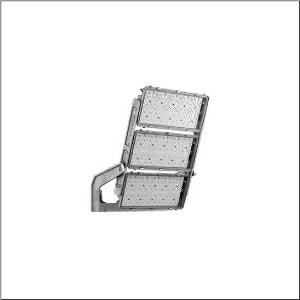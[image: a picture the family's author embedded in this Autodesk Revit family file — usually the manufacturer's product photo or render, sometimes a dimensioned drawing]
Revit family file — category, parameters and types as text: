
# Revit family: floodlight_fl_11_maxi_pro_remote___pl33t_5xa779427f01ba_72f0
name_source: partatom
category: Lighting Fixtures
units: mm (PartAtom-declared; Revit-internal decimal feet)

## family parameters
Cut with Voids When Loaded = No
Host = Face
Light Source = No
Part Type = Normal
Room Calculation Point = No
Round Connector Dimension = Use Diameter
Shared = No

## types (1)
- --- (1 x LED, 132850 lm, 953.7 W, 5000K)
    Apparent Load = 954 VA
    CIE Flux Codes = 25 74 99 100 100
    Color Rendering = 70
    Color Temperature = 5000K
    Default Elevation = 1800 mm
    Description = Floodlight FL 11  maxi  pro Remote floodlight; light control with lens of PMMA; cover panel of toughened safety glass, transparent; light distribution: PL33T, asymmetric direct distribution, LED; colour temperature: 5000K, rated luminous flux: 132.850lm, colour rendering: CRI > 70, light colour: 750; luminous efficacy: 139lm/W; brightness control: DALI 2 (1 DALI address); with terminal, 8-pole, max. 2.5mm², mains connection: 220..240V/380..400V AC, 50/60Hz, surge voltage resistance: line to ground: 10kV, ECG replaceable separately, no afterglow with DALI off / DMX off command, LED unit replaceable without ESD environment, dustproof LED module, dimming range 10..100%; 954W floodlight with 2x LED unit of diecast aluminium, coated grey; length: 713mm / width: 651mm / height: 338mm; mounting bracket, of diecast aluminium, uncoated, natural, equipment: Longlife, protection rating (complete): IP66; insulation class (complete): insulation class I (protective earthing); certification: CE, ENEC, VDE; ball protection: ball impact resistance with accessories, impact resistance: IK07; only for outdoor installations, rated ambient temperature 10°C, permissible operating ambient temperature: -40..+30°C, permissible storage temperature: -40..+85°Cpackaging unit: 1 piece

Light Distribution: PL33T
    Height = 320 mm
    Lamp = 1 x LED
    Lamp Light Flux = 132850 lm
    Lamp Power = 953.7 W
    Lamp count = 1
    Length = 1002 mm
    Luminous efficacy = 139 lm/W
    Manufacturer = Siteco
    ModVariant = No
    Model = 5XA779427F01BA
    Mounting Place = Ceiling
    Mounting Type = Surface mounted
    Number of Poles = 1
    OnlyDefault = Yes
    Power Factor = 1
    Product Name = Floodlight FL 11 maxi pro Remote | PL33T
    Product group = floodlight | ceiling mounted
    ProductGroupID = 302
    Protection Class = Protection class I
    Protection Degree = IP 66
    RLX_Detail_Level = 1
    RLX_Emergency_Light_Flux = 0 lm
    RLX_Emergency_Type = 0
    RLX_Emergency_Type_DB = No
    RlxData = <blob elided: 52289 chars, md5=9290f567>
    Socket = socket
    Standby Power = 0 W
    System Light Flux = 132850 lm
    System Power = 954 W
    Type Comments = factory setting: luminous flux: 100 % | dim-lin: 254 | 665 mA
    Type Image = l_1349141.jpg
    URL = http://relux.com
    VarID = @adj_118529
    Voltage = 0 V
    Weight = 0.00 kg
    Width = 655 mm

## geometry (parser evidence)
native form markers: Blend x4, Sweep x12
no freeform markers — native parametric forms only
